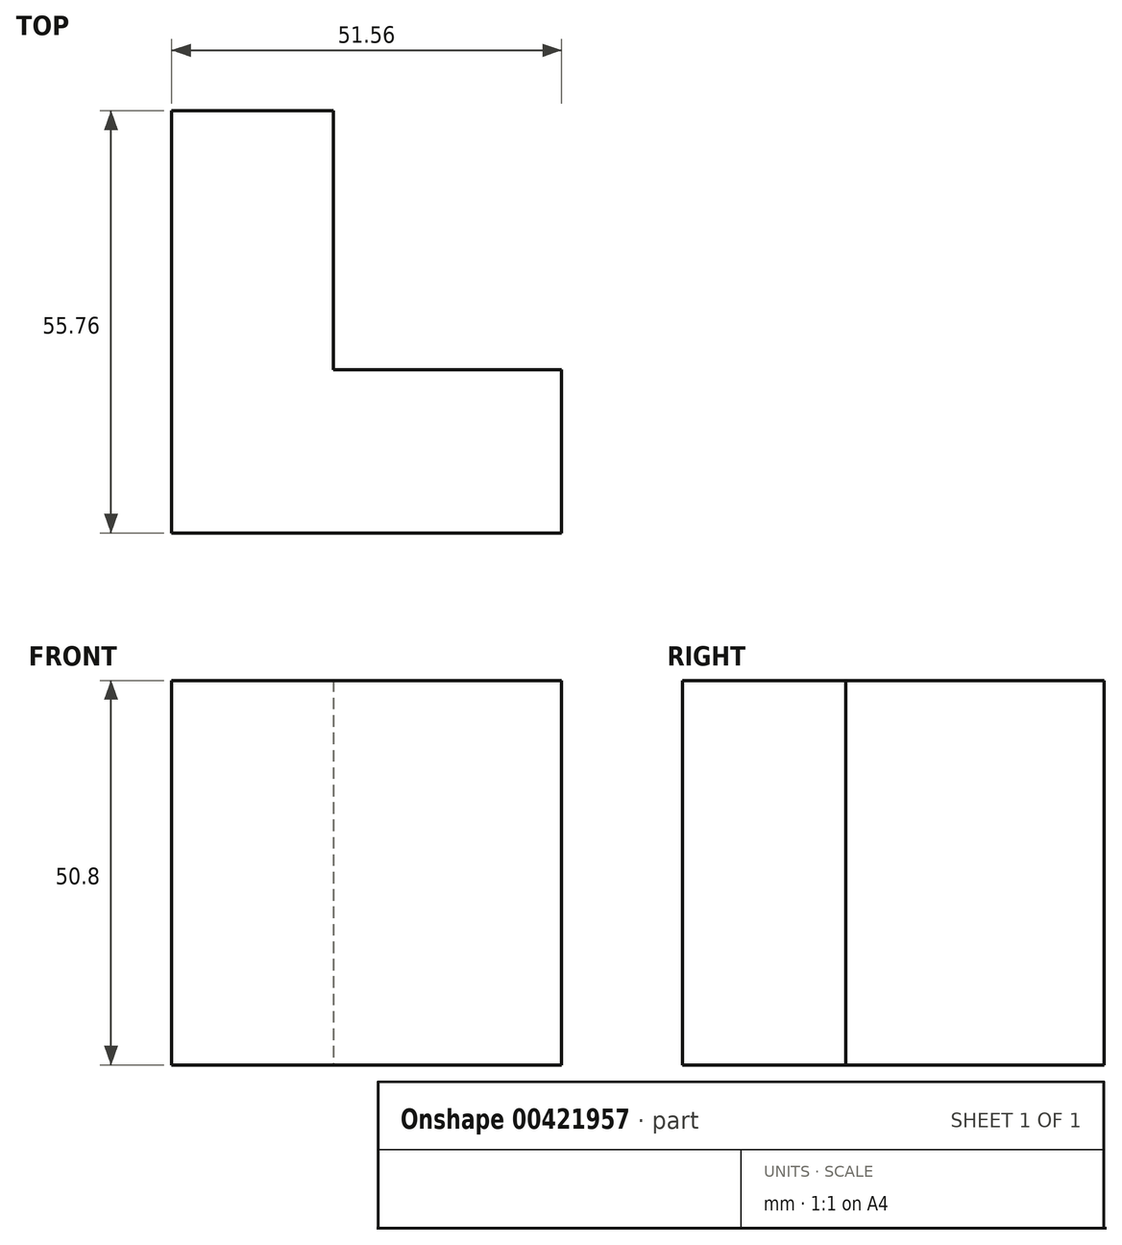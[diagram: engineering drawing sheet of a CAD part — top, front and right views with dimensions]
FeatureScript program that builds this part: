
annotation { "Feature Type Name" : "Feature", "Feature Type Description" : "" }
export const myFeature = defineFeature(function(context is Context, id is Id, definition is map)
    precondition{}
    {
        {
            var Q0;
            Q0=qCreatedBy(makeId("Top.planeOp"),FACE);
            var sketch = newSketch(context, id + "F0", { "sketchPlane" : qUnion([Q0])});
            skLineSegment(sketch, "E0", {"start": v(0, 0) * mm, "end": v(-47.93, 0) * mm});
            skLineSegment(sketch, "E1", {"start": v(-47.93, 0) * mm, "end": v(-47.93, 55.76) * mm});
            skLineSegment(sketch, "E2", {"start": v(-47.93, 55.76) * mm, "end": v(-26.54, 55.76) * mm});
            skLineSegment(sketch, "E3", {"start": v(-26.54, 55.76) * mm, "end": v(-26.54, 24.63) * mm});
            skLineSegment(sketch, "E4", {"start": v(-26.54, 24.63) * mm, "end": v(-26.54, 21.58) * mm});
            skLineSegment(sketch, "E5", {"start": v(-26.54, 21.58) * mm, "end": v(3.63, 21.58) * mm});
            skLineSegment(sketch, "E6", {"start": v(3.63, 21.58) * mm, "end": v(3.63, 0) * mm});
            skLineSegment(sketch, "E7", {"start": v(3.63, 0) * mm, "end": v(0, 0) * mm});
            skSolve(sketch);
        }
        {
            var Q0;
            Q0=makeQuery(id+"F0.imprint","IMPRINT",FACE,{"disambiguationData":[TD([[makeQuery(id+"F0.imprint","IMPRINT",EDGE,{"derivedFrom":sQuery(id+"F0.wireOp",EDGE,"E0")}),-1.0]])]});
            extrude(context, id + "F1", {"entities" : qUnion([Q0]), "depth" : 50.8 * mm});
        }
    });
